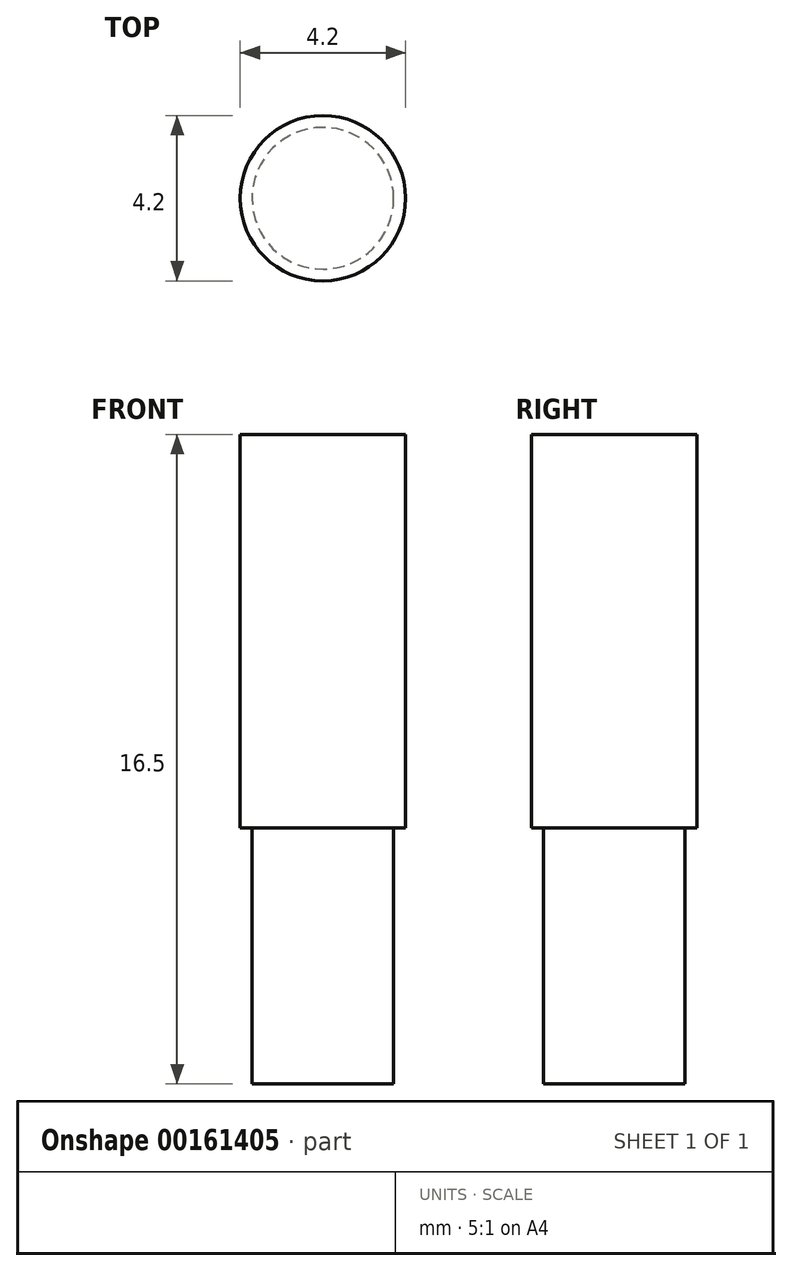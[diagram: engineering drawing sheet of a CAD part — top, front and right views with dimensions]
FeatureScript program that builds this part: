
annotation { "Feature Type Name" : "Feature", "Feature Type Description" : "" }
export const myFeature = defineFeature(function(context is Context, id is Id, definition is map)
    precondition{}
    {
        {
            var Q0;
            Q0=qCreatedBy(makeId("Top.planeOp"),FACE);
            var sketch = newSketch(context, id + "F0", { "sketchPlane" : qUnion([Q0])});
            skCircle(sketch, "E0", {"center": v(0, 0) * mm, "radius": 2.1 * mm});
            skSolve(sketch);
        }
        {
            var Q0;
            Q0 = qSketchRegion(id + "F0", true);
            extrude(context, id + "F1", {"entities" : qUnion([Q0]), "oppositeDirection" : true, "depth" : 10 * mm});
        }
        {
            var Q0;
            Q0=makeQuery(id+"F1.opExtrude","CAP_FACE",FACE,{"disambiguationData":[OSD([sQuery(id+"F0.wireOp",EDGE,"E0")])],"isStart":false});
            var sketch = newSketch(context, id + "F2", { "sketchPlane" : qUnion([Q0])});
            skCircle(sketch, "E1", {"center": v(0, 0) * mm, "radius": 1.8 * mm});
            skSolve(sketch);
        }
        {
            var Q0;
            Q0 = qSketchRegion(id + "F2", true);
            extrude(context, id + "F3", {"entities" : qUnion([Q0]), "operationType" : NewBodyOperationType.ADD, "depth" : 6.5 * mm});
        }
    });
